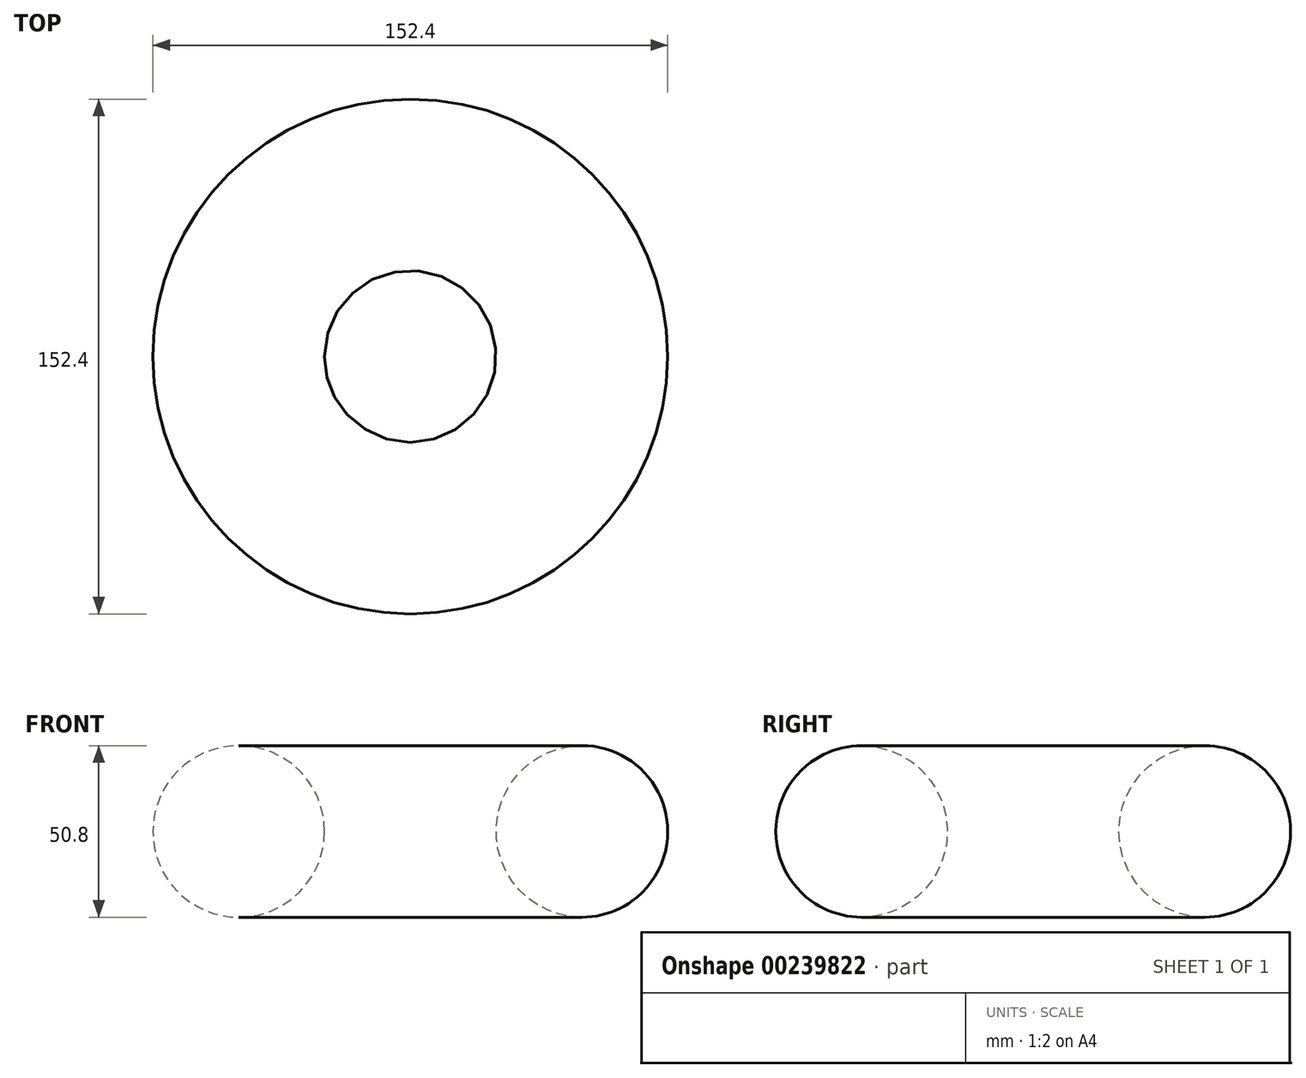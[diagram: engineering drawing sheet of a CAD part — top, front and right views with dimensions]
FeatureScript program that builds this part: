
annotation { "Feature Type Name" : "Feature", "Feature Type Description" : "" }
export const myFeature = defineFeature(function(context is Context, id is Id, definition is map)
    precondition{}
    {
        {
            var Q0;
            Q0=qCreatedBy(makeId("Front.planeOp"),FACE);
            var sketch = newSketch(context, id + "F0", { "sketchPlane" : qUnion([Q0])});
            skCircle(sketch, "E0", {"center": v(-50.8, 0) * mm, "radius": 25.4 * mm});
            skLineSegment(sketch, "E1", {"start": v(0, 0) * mm, "end": v(0, 95.28) * mm, "construction": true});
            skSolve(sketch);
        }
        {
            var Q0;
            Q0 = qSketchRegion(id + "F0", true);
            var Q1;
            Q1=sQuery(id+"F0.wireOp",EDGE,"E1");
            revolve(context, id + "F1", {"entities" : qUnion([Q0]), "axis" : qUnion([Q1]), "revolveType" : RevolveType.FULL});
        }
    });
